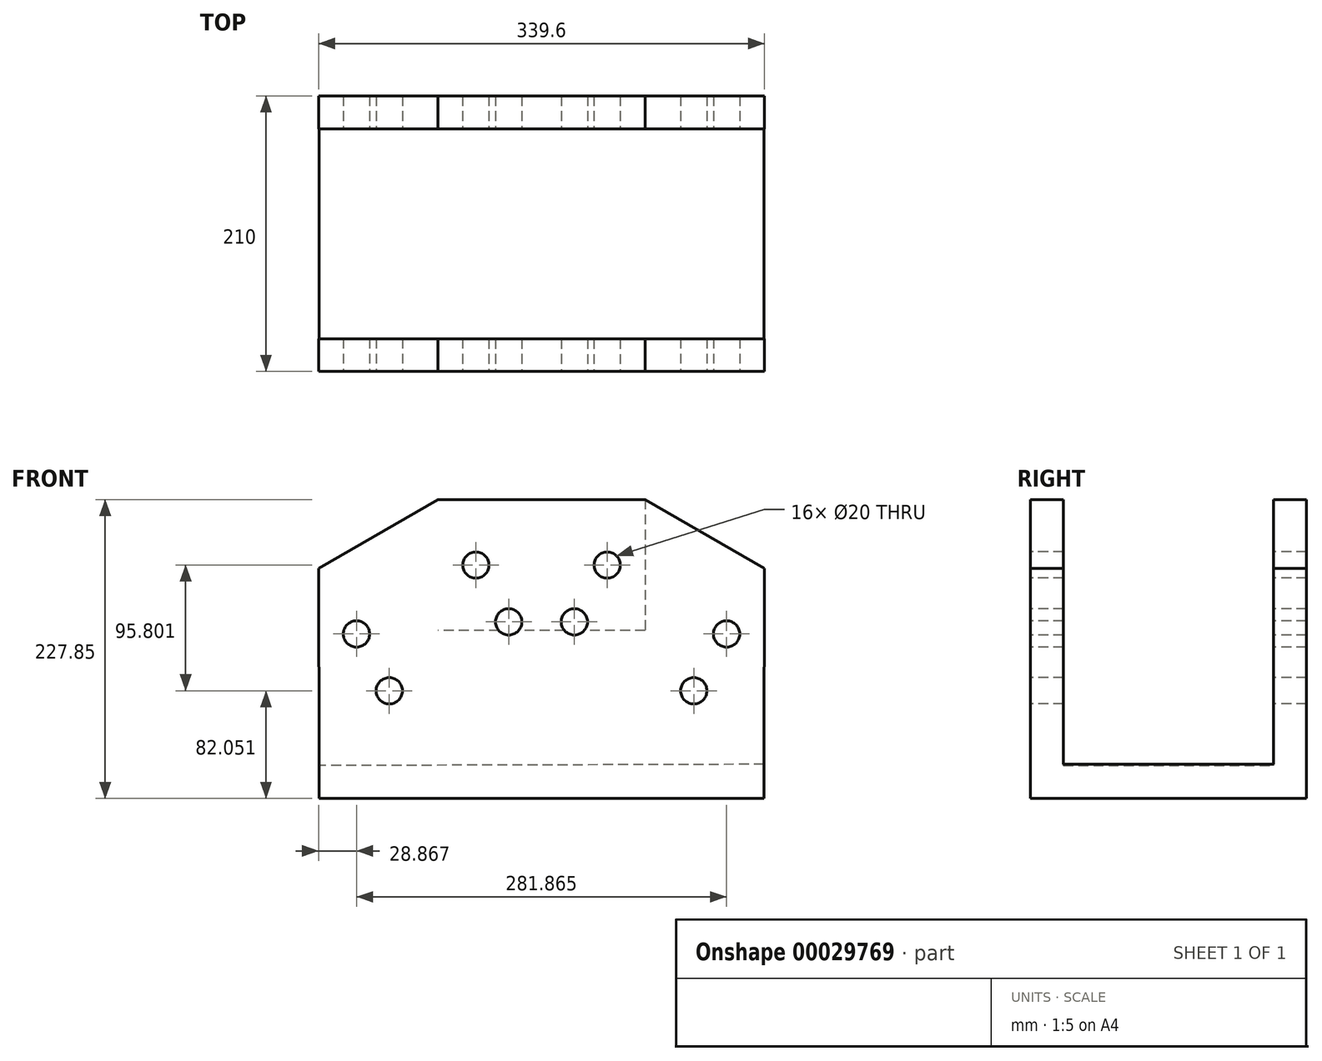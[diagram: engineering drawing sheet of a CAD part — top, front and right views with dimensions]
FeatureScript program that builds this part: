
annotation { "Feature Type Name" : "Feature", "Feature Type Description" : "" }
export const myFeature = defineFeature(function(context is Context, id is Id, definition is map)
    precondition{}
    {
        {
            var Q0;
            Q0=qCreatedBy(makeId("Front.planeOp"),FACE);
            var sketch = newSketch(context, id + "F0", { "sketchPlane" : qUnion([Q0])});
            skLineSegment(sketch, "E0", {"start": v(0, 0) * mm, "end": v(0, 202.85) * mm});
            skCircle(sketch, "E1", {"center": v(-25, 109.55) * mm, "radius": 10 * mm});
            skCircle(sketch, "E2", {"center": v(-50, 152.85) * mm, "radius": 10 * mm});
            skLineSegment(sketch, "E3", {"start": v(0, 0) * mm, "end": v(-169.37, 0) * mm});
            skCircle(sketch, "E4", {"center": v(-115.93, 57.05) * mm, "radius": 10 * mm});
            skCircle(sketch, "E5", {"center": v(-140.93, 100.35) * mm, "radius": 10 * mm});
            skLineSegment(sketch, "E6", {"start": v(0, 202.85) * mm, "end": v(-78.87, 202.85) * mm});
            skLineSegment(sketch, "E7", {"start": v(-169.8, 150.35) * mm, "end": v(-169.37, 0) * mm});
            skLineSegment(sketch, "E8", {"start": v(-169.8, 150.35) * mm, "end": v(-78.87, 202.85) * mm});
            skLineSegment(sketch, "E9.MirrorCS", {"start": v(0, 0) * mm, "end": v(169.37, 0) * mm});
            skLineSegment(sketch, "E10.MirrorCS", {"start": v(169.8, 150.35) * mm, "end": v(169.37, 0) * mm});
            skLineSegment(sketch, "E11.MirrorCS", {"start": v(169.8, 150.35) * mm, "end": v(78.87, 202.85) * mm});
            skLineSegment(sketch, "E12.MirrorCS", {"start": v(0, 202.85) * mm, "end": v(78.87, 202.85) * mm});
            skCircle(sketch, "E13.MirrorC", {"center": v(50, 152.85) * mm, "radius": 10 * mm});
            skCircle(sketch, "E14.MirrorC", {"center": v(25, 109.55) * mm, "radius": 10 * mm});
            skCircle(sketch, "E15.MirrorC", {"center": v(115.93, 57.05) * mm, "radius": 10 * mm});
            skCircle(sketch, "E16.MirrorC", {"center": v(140.93, 100.35) * mm, "radius": 10 * mm});
            skLineSegment(sketch, "E17", {"start": v(-169.37, 0) * mm, "end": v(-169.37, -25) * mm});
            skLineSegment(sketch, "E18", {"start": v(-169.37, -25) * mm, "end": v(169.37, -25) * mm});
            skLineSegment(sketch, "E19", {"start": v(169.37, -25) * mm, "end": v(169.37, 0) * mm});
            skSolve(sketch);
        }
        {
            var Q0;
            Q0=makeQuery(id+"F0.imprint","IMPRINT",FACE,{"disambiguationData":[TD([[makeQuery(id+"F0.imprint","IMPRINT",EDGE,{"derivedFrom":sQuery(id+"F0.wireOp",EDGE,"E0")}),1.0]])]});
            var Q1;
            Q1=makeQuery(id+"F0.imprint","IMPRINT",FACE,{"disambiguationData":[TD([[makeQuery(id+"F0.imprint","IMPRINT",EDGE,{"derivedFrom":sQuery(id+"F0.wireOp",EDGE,"E0")}),-1.0]])]});
            var Q2;
            Q2=makeQuery(id+"F0.imprint","IMPRINT",FACE,{"disambiguationData":[TD([[makeQuery(id+"F0.imprint","IMPRINT",EDGE,{"derivedFrom":sQuery(id+"F0.wireOp",EDGE,"E3")}),1.0]])]});
            extrude(context, id + "F1", {"entities" : qUnion([Q0, Q1, Q2]), "oppositeDirection" : true, "depth" : 25 * mm});
        }
        {
            var Q0;
            Q0=makeQuery(id+"F1.opExtrude","CAP_FACE",FACE,{"disambiguationData":[OSD([sQuery(id+"F0.wireOp",EDGE,"E1"),sQuery(id+"F0.wireOp",EDGE,"E2"),sQuery(id+"F0.wireOp",EDGE,"E4"),sQuery(id+"F0.wireOp",EDGE,"E5"),sQuery(id+"F0.wireOp",EDGE,"E6"),sQuery(id+"F0.wireOp",EDGE,"E7"),sQuery(id+"F0.wireOp",EDGE,"E8"),sQuery(id+"F0.wireOp",EDGE,"E10.MirrorCS"),sQuery(id+"F0.wireOp",EDGE,"E11.MirrorCS"),sQuery(id+"F0.wireOp",EDGE,"E12.MirrorCS"),sQuery(id+"F0.wireOp",EDGE,"E13.MirrorC"),sQuery(id+"F0.wireOp",EDGE,"E14.MirrorC"),sQuery(id+"F0.wireOp",EDGE,"E15.MirrorC"),sQuery(id+"F0.wireOp",EDGE,"E16.MirrorC"),sQuery(id+"F0.wireOp",EDGE,"E17"),sQuery(id+"F0.wireOp",EDGE,"E18"),sQuery(id+"F0.wireOp",EDGE,"E19")])],"isStart":true});
            var sketch = newSketch(context, id + "F2", { "sketchPlane" : qUnion([Q0])});
            skLineSegment(sketch, "E20", {"start": v(-169.37, -25) * mm, "end": v(-169.37, 0) * mm});
            skLineSegment(sketch, "E21", {"start": v(-169.37, 0) * mm, "end": v(169.37, 0) * mm});
            skSolve(sketch);
        }
        {
            var Q0;
            Q0=makeQuery(id+"F2.imprint","IMPRINT",FACE,{"disambiguationData":[TD([[makeQuery(id+"F2.imprint","IMPRINT",EDGE,{"derivedFrom":sQuery(id+"F2.wireOp",EDGE,"E21")}),1.0]])]});
            extrude(context, id + "F3", {"entities" : qUnion([Q0]), "operationType" : NewBodyOperationType.ADD, "depth" : 185 * mm});
        }
        {
            var Q0;
            Q0=makeQuery(id+"F3.opExtrude","CAP_FACE",FACE,{"disambiguationData":[OSD([sQuery(id+"F0.wireOp",EDGE,"E1"),sQuery(id+"F0.wireOp",EDGE,"E2"),sQuery(id+"F0.wireOp",EDGE,"E4"),sQuery(id+"F0.wireOp",EDGE,"E5"),sQuery(id+"F0.wireOp",EDGE,"E6"),sQuery(id+"F0.wireOp",EDGE,"E7"),sQuery(id+"F0.wireOp",EDGE,"E8"),sQuery(id+"F0.wireOp",EDGE,"E10.MirrorCS"),sQuery(id+"F0.wireOp",EDGE,"E11.MirrorCS"),sQuery(id+"F0.wireOp",EDGE,"E12.MirrorCS"),sQuery(id+"F0.wireOp",EDGE,"E13.MirrorC"),sQuery(id+"F0.wireOp",EDGE,"E14.MirrorC"),sQuery(id+"F0.wireOp",EDGE,"E15.MirrorC"),sQuery(id+"F0.wireOp",EDGE,"E16.MirrorC"),sQuery(id+"F2.wireOp",EDGE,"E21")])],"isStart":false});
            extrude(context, id + "F4", {"entities" : qUnion([Q0]), "operationType" : NewBodyOperationType.ADD, "oppositeDirection" : true, "depth" : 25 * mm});
        }
        {
            var Q0;
            {var subQ0=sQuery(id+"F0.wireOp",EDGE,"E7");Q0=makeQuery(id+"F3.boolean.opBoolean","MERGE",FACE,{"derivedFrom":[makeQuery(id+"F1.opExtrude","SWEPT_FACE",FACE,{"disambiguationData":[OSD([subQ0])]}),makeQuery(id+"F3.opExtrude","SWEPT_FACE",FACE,{"disambiguationData":[OSD([subQ0])]})]});}
            var sketch = newSketch(context, id + "F5", { "sketchPlane" : qUnion([Q0])});
            skLineSegment(sketch, "E22", {"start": v(185, 0.49) * mm, "end": v(160, 0.49) * mm});
            skLineSegment(sketch, "E23", {"start": v(160, 0.49) * mm, "end": v(0, 0.49) * mm});
            skLineSegment(sketch, "E24", {"start": v(160, 0.49) * mm, "end": v(160, 150.84) * mm});
            skLineSegment(sketch, "E25", {"start": v(160, 150.84) * mm, "end": v(0, 150.84) * mm});
            skLineSegment(sketch, "E26", {"start": v(0, 150.84) * mm, "end": v(0, 0.49) * mm});
            skSolve(sketch);
        }
        {
            var Q0;
            Q0=makeQuery(id+"F5.imprint","IMPRINT",FACE,{"disambiguationData":[TD([[makeQuery(id+"F5.imprint","IMPRINT",EDGE,{"derivedFrom":sQuery(id+"F5.wireOp",EDGE,"E23")}),-1.0]])]});
            extrude(context, id + "F6", {"entities" : qUnion([Q0]), "operationType" : NewBodyOperationType.REMOVE, "oppositeDirection" : true, "depth" : 400 * mm});
        }
        {
            var Q0;
            Q0=makeQuery(id+"F1.opExtrude","CAP_FACE",FACE,{"disambiguationData":[OSD([sQuery(id+"F0.wireOp",EDGE,"E1"),sQuery(id+"F0.wireOp",EDGE,"E2"),sQuery(id+"F0.wireOp",EDGE,"E4"),sQuery(id+"F0.wireOp",EDGE,"E5"),sQuery(id+"F0.wireOp",EDGE,"E6"),sQuery(id+"F0.wireOp",EDGE,"E7"),sQuery(id+"F0.wireOp",EDGE,"E8"),sQuery(id+"F0.wireOp",EDGE,"E10.MirrorCS"),sQuery(id+"F0.wireOp",EDGE,"E11.MirrorCS"),sQuery(id+"F0.wireOp",EDGE,"E12.MirrorCS"),sQuery(id+"F0.wireOp",EDGE,"E13.MirrorC"),sQuery(id+"F0.wireOp",EDGE,"E14.MirrorC"),sQuery(id+"F0.wireOp",EDGE,"E15.MirrorC"),sQuery(id+"F0.wireOp",EDGE,"E16.MirrorC"),sQuery(id+"F0.wireOp",EDGE,"E17"),sQuery(id+"F0.wireOp",EDGE,"E18"),sQuery(id+"F0.wireOp",EDGE,"E19")])],"isStart":true});
            extrude(context, id + "F7", {"entities" : qUnion([Q0]), "operationType" : NewBodyOperationType.ADD, "depth" : 185 * mm});
        }
        {
            var Q0;
            {var subQ0=sQuery(id+"F0.wireOp",EDGE,"E8");Q0=makeQuery(id+"F3.boolean.opBoolean","MERGE",FACE,{"derivedFrom":[makeQuery(id+"F1.opExtrude","SWEPT_FACE",FACE,{"disambiguationData":[OSD([subQ0])]}),makeQuery(id+"F3.opExtrude","SWEPT_FACE",FACE,{"disambiguationData":[OSD([subQ0])]})]});}
            var sketch = newSketch(context, id + "F8", { "sketchPlane" : qUnion([Q0])});
            skLineSegment(sketch, "E27", {"start": v(-71.88, -160) * mm, "end": v(33.12, -160) * mm});
            skLineSegment(sketch, "E28", {"start": v(-71.88, 0) * mm, "end": v(33.12, 0) * mm});
            skSolve(sketch);
        }
        {
            var Q0;
            Q0 = qSketchRegion(id + "F8", true);
            var Q1;
            {var subQ4=sQuery(id+"F8.wireOp",EDGE,"E27");Q1=makeQuery(id+"F8.imprint","IMPRINT",FACE,{"disambiguationData":[TD([[makeQuery(id+"F8.imprint","IMPRINT",EDGE,{"derivedFrom":subQ4}),1.0]])]});}
            extrude(context, id + "F9", {"entities" : qUnion([Q0, Q1]), "operationType" : NewBodyOperationType.REMOVE, "oppositeDirection" : true, "depth" : 100 * mm});
        }
        {
            var Q0;
            {var subQ0=sQuery(id+"F0.wireOp",EDGE,"E11.MirrorCS");Q0=makeQuery(id+"F3.boolean.opBoolean","MERGE",FACE,{"derivedFrom":[makeQuery(id+"F1.opExtrude","SWEPT_FACE",FACE,{"disambiguationData":[OSD([subQ0])]}),makeQuery(id+"F3.opExtrude","SWEPT_FACE",FACE,{"disambiguationData":[OSD([subQ0])]})]});}
            var sketch = newSketch(context, id + "F10", { "sketchPlane" : qUnion([Q0])});
            skLineSegment(sketch, "E29", {"start": v(71.88, -160) * mm, "end": v(-33.12, -160) * mm});
            skLineSegment(sketch, "E30", {"start": v(71.88, 0) * mm, "end": v(-33.12, 0) * mm});
            skSolve(sketch);
        }
        {
            var Q0;
            {var subQ0=sQuery(id+"F0.wireOp",EDGE,"E6");var subQ1=sQuery(id+"F0.wireOp",EDGE,"E12.MirrorCS");Q0=makeQuery(id+"F3.boolean.opBoolean","MERGE",FACE,{"derivedFrom":[makeQuery(id+"F1.opExtrude","SWEPT_FACE",FACE,{"disambiguationData":[OSD([subQ0,subQ1])]}),makeQuery(id+"F3.opExtrude","SWEPT_FACE",FACE,{"disambiguationData":[OSD([subQ0,subQ1])]})]});}
            var sketch = newSketch(context, id + "F11", { "sketchPlane" : qUnion([Q0])});
            skLineSegment(sketch, "E31", {"start": v(78.87, 0) * mm, "end": v(-78.87, 0) * mm});
            skLineSegment(sketch, "E32", {"start": v(78.87, -160.3) * mm, "end": v(-78.87, -160) * mm});
            skSolve(sketch);
        }
        {
            var Q0;
            Q0 = qSketchRegion(id + "F11", true);
            var Q1;
            {var subQ0=sQuery(id+"F0.wireOp",EDGE,"E11.MirrorCS");var subQ7=makeQuery(id+"F6.boolean.opBoolean","INTERSECT",EDGE,{"derivedFrom":[makeQuery(id+"F3.boolean.opBoolean","MERGE",FACE,{"derivedFrom":[makeQuery(id+"F1.opExtrude","SWEPT_FACE",FACE,{"disambiguationData":[OSD([subQ0])]}),makeQuery(id+"F3.opExtrude","SWEPT_FACE",FACE,{"disambiguationData":[OSD([subQ0])]})]}),makeQuery(id+"F6.opExtrude","SWEPT_FACE",FACE,{"disambiguationData":[OSD([sQuery(id+"F5.wireOp",EDGE,"E25")])]})]});Q1=makeQuery(id+"F10.imprint","IMPRINT",FACE,{"disambiguationData":[TD([[makeQuery(id+"F10.imprint","IMPRINT",EDGE,{"derivedFrom":subQ7}),1.0]])]});}
            extrude(context, id + "F12", {"entities" : qUnion([Q0, Q1]), "operationType" : NewBodyOperationType.REMOVE, "oppositeDirection" : true, "depth" : 100 * mm});
        }
        {
            var Q0;
            {var subQ5=sQuery(id+"F11.wireOp",EDGE,"E31");Q0=makeQuery(id+"F11.imprint","IMPRINT",FACE,{"disambiguationData":[TD([[makeQuery(id+"F11.imprint","IMPRINT",EDGE,{"derivedFrom":subQ5}),1.0]])]});}
            extrude(context, id + "F13", {"entities" : qUnion([Q0]), "operationType" : NewBodyOperationType.REMOVE, "oppositeDirection" : true, "depth" : 100 * mm});
        }
    });
